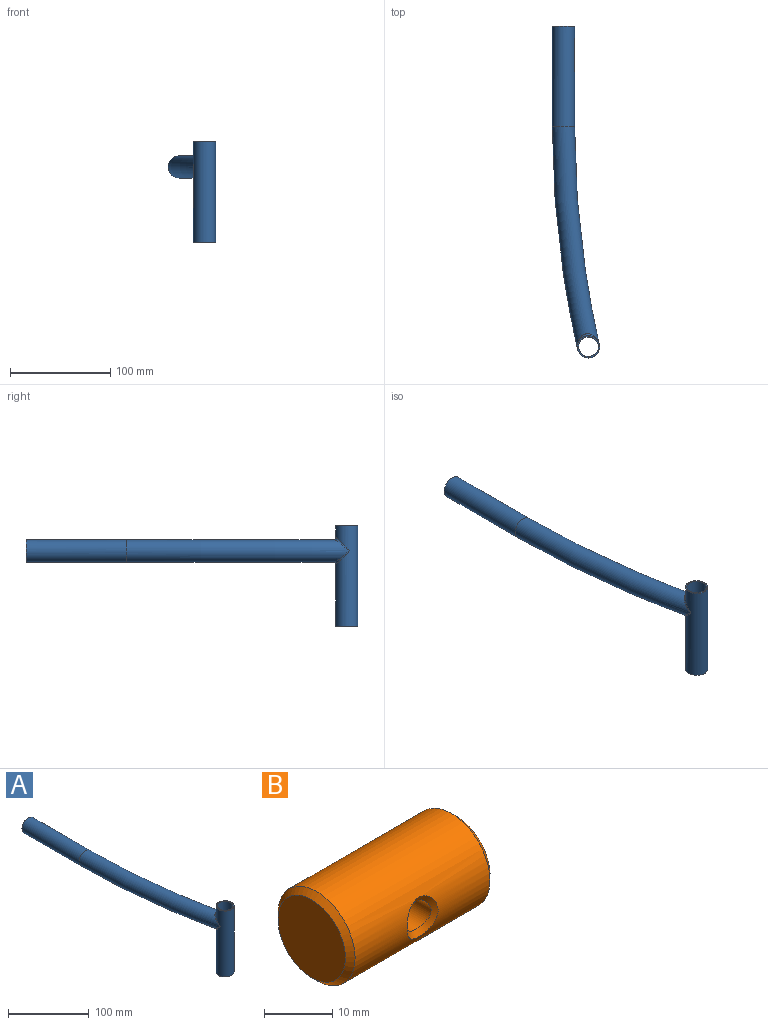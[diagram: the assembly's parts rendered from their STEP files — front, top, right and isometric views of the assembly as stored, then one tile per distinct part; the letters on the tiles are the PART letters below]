
ASSEMBLY  parts=2 mates=1
PART A: 16 faces, bbox 53.6x331.1x100 mm
  f0: torus R=980.5mm, axis (0,0,1), area 14894.3mm2, adj f4,f14,f15
  f1: cylinder r=9.75mm len=100mm, axis (0,-1,0), area 5926.7mm2, adj f2,f3,f5,f6,f7,f8
  f2: torus R=980.5mm, axis (0,0,1), area 13084.4mm2, adj f1,f13
  f3: plane 22.2x22.2mm, normal (0,1,0), area 88.4mm2, adj f1,f4
  f4: cylinder r=11.1mm len=100mm, axis (0,-1,0), area 6775.7mm2, adj f0,f3,f5,f6,f7,f8
  f5: cylinder r=3mm len=6mm, axis (1,0,0), area 13mm2, adj f1,f4,f6,f8
  f6: plane 28x1.41mm, normal (0,0,1), area 39.5mm2, adj f1,f4,f5,f7
  f7: cylinder r=3mm len=6mm, axis (1,0,0), area 13mm2, adj f1,f4,f6,f8
  f8: plane 28x1.41mm, normal (0,0,-1), area 39.5mm2, adj f1,f4,f5,f7
  f9: plane 22.2x22.2mm, normal (0,0,-1), area 88.4mm2, adj f11,f12
  f10: plane 22.2x22.2mm, normal (0,0,1), area 88.4mm2, adj f11,f12
  f11: cylinder r=9.75mm len=100mm, axis (0,0,-1), area 6126.1mm2, adj f9,f10
  f12: cylinder r=11.1mm len=100mm, axis (0,0,-1), area 6392.7mm2, adj f9,f10,f14,f15
  f13: cylinder r=11.1mm len=19.5mm, axis (0,0,-1), area 343.4mm2, adj f2
  f14: bspline ~22.03x15.51mm, area 78.1mm2, adj f0,f12
  f15: bspline ~22.03x15.52mm, area 78.1mm2, adj f0,f12
PART B: 8 faces, bbox 30x16x16 mm
  f0: cylinder r=8mm len=28mm, axis (-1,0,0), area 1333.7mm2, adj f3,f4,f6,f7
  f1: plane 14x14mm, normal (1,0,0), area 153.9mm2, adj f4
  f2: plane 14x14mm, normal (-1,0,0), area 153.9mm2, adj f3
  f3: cone r=8mm half-angle=45deg, axis (1,0,0), area 66.6mm2, adj f0,f2
  f4: cone r=7mm half-angle=45deg, axis (-1,0,0), area 66.6mm2, adj f0,f1
  f5: cylinder r=2.5mm len=13.05mm, axis (0,-1,0), area 204.9mm2, adj f6,f7
  f6: bspline ~7.08x6.44mm, area 21.2mm2, adj f0,f5
  f7: bspline ~7.08x6.44mm, area 21.2mm2, adj f0,f5
PLACE A t=(-24.74,65.55,-1.13)mm fixed
PLACE B rot(axis=(0,0,1),90deg) t=(-24.74,150.55,-1.13)mm
MATE fastened B.f0 <-> A.f1  axis (0,1,0) through (-24.74,164.55,-1.13)mm
